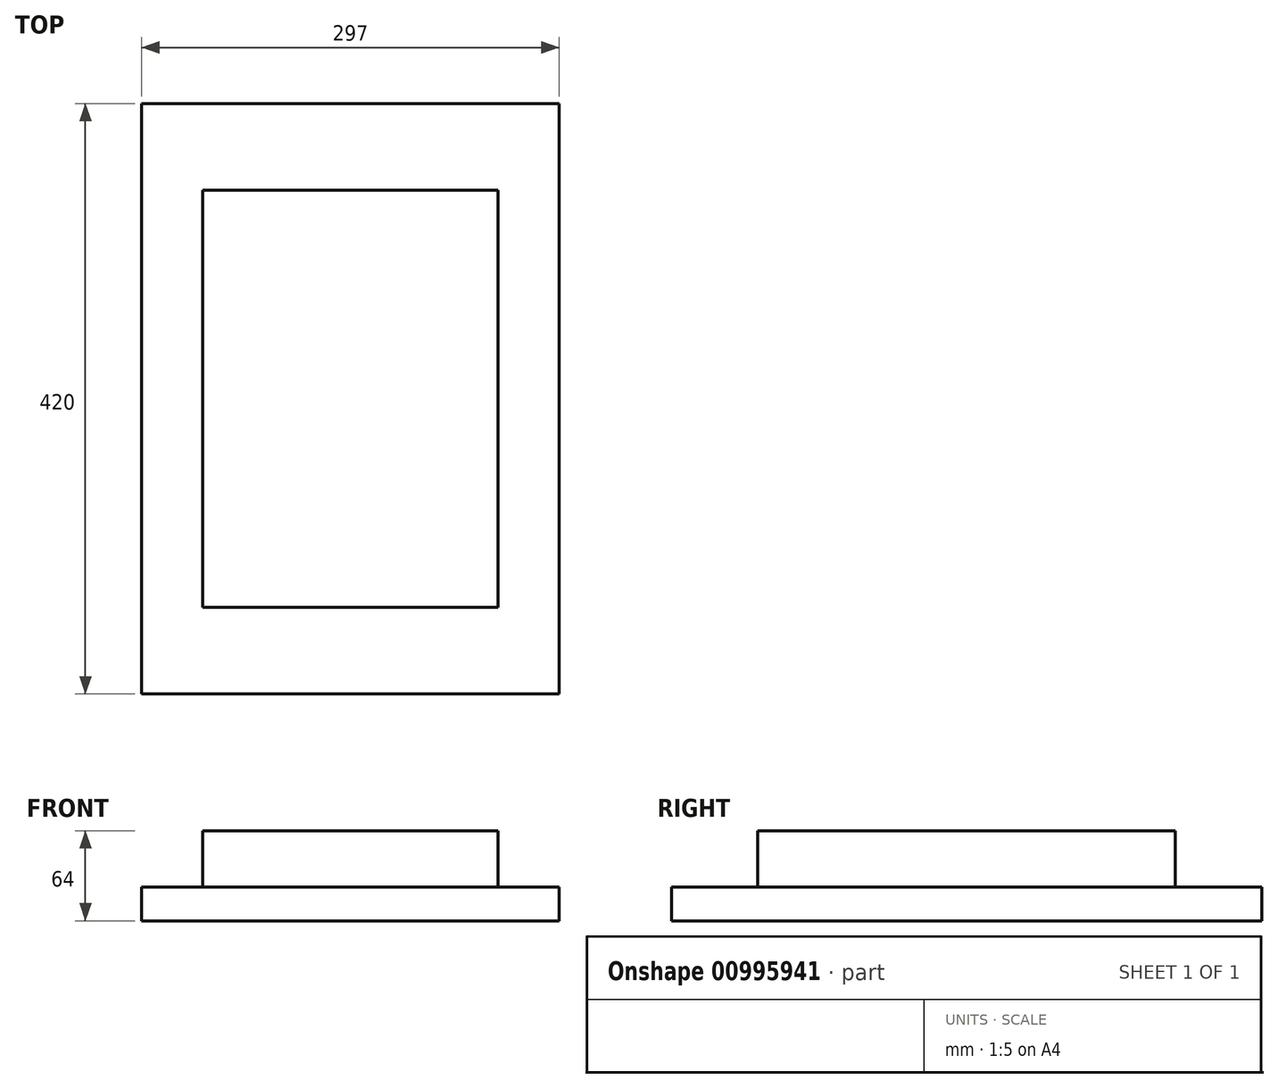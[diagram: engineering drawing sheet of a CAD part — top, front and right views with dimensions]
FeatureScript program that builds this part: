
annotation { "Feature Type Name" : "Feature", "Feature Type Description" : "" }
export const myFeature = defineFeature(function(context is Context, id is Id, definition is map)
    precondition{}
    {
        {
            var Q0;
            Q0=qCreatedBy(makeId("Top.planeOp"),FACE);
            var sketch = newSketch(context, id + "F0", { "sketchPlane" : qUnion([Q0])});
            skLineSegment(sketch, "E0.bottom", {"start": v(105, 148.5) * mm, "end": v(-105, 148.5) * mm});
            skLineSegment(sketch, "E0.top", {"start": v(105, -148.5) * mm, "end": v(-105, -148.5) * mm});
            skLineSegment(sketch, "E0.left", {"start": v(105, 148.5) * mm, "end": v(105, -148.5) * mm});
            skLineSegment(sketch, "E0.right", {"start": v(-105, 148.5) * mm, "end": v(-105, -148.5) * mm});
            skPoint(sketch, "E0.middle", {"position": v(0, 0) * mm});
            skSolve(sketch);
        }
        {
            var Q0;
            Q0=makeQuery(id+"F0.imprint","IMPRINT",FACE,{"disambiguationData":[TD([[makeQuery(id+"F0.imprint","IMPRINT",EDGE,{"derivedFrom":sQuery(id+"F0.wireOp",EDGE,"E0.bottom")}),1.0]])]});
            extrude(context, id + "F1", {"entities" : qUnion([Q0]), "depth" : 40 * mm, "offsetDistance" : 25 * mm});
        }
        {
            var Q0;
            Q0=qCreatedBy(makeId("Top.planeOp"),FACE);
            var sketch = newSketch(context, id + "F2", { "sketchPlane" : qUnion([Q0])});
            skLineSegment(sketch, "E1.bottom", {"start": v(148.5, 210) * mm, "end": v(-148.5, 210) * mm});
            skLineSegment(sketch, "E1.top", {"start": v(148.5, -210) * mm, "end": v(-148.5, -210) * mm});
            skLineSegment(sketch, "E1.left", {"start": v(148.5, 210) * mm, "end": v(148.5, -210) * mm});
            skLineSegment(sketch, "E1.right", {"start": v(-148.5, 210) * mm, "end": v(-148.5, -210) * mm});
            skPoint(sketch, "E1.middle", {"position": v(0, 0) * mm});
            skSolve(sketch);
        }
        {
            var Q0;
            Q0 = qSketchRegion(id + "F2", true);
            extrude(context, id + "F3", {"entities" : qUnion([Q0]), "oppositeDirection" : true, "depth" : 24 * mm, "offsetDistance" : 25 * mm});
        }
    });
